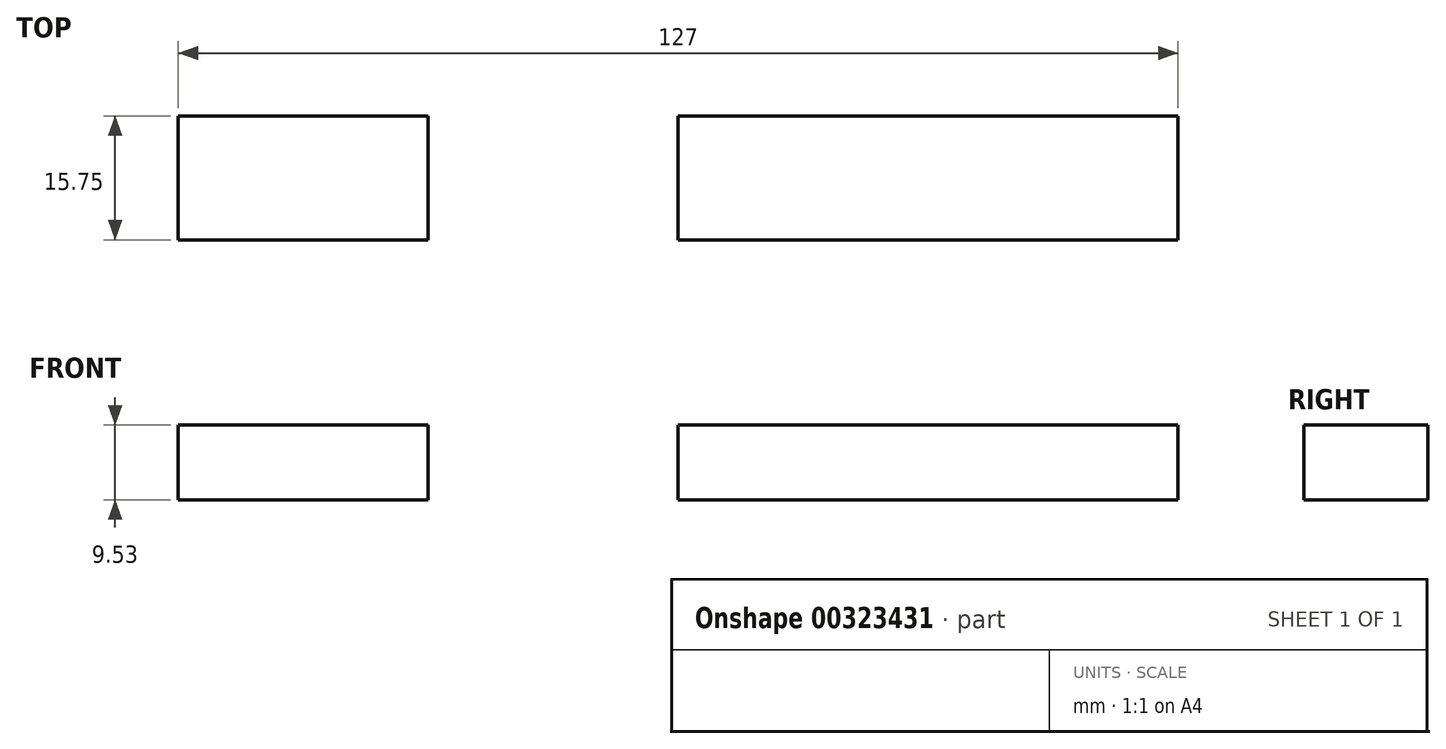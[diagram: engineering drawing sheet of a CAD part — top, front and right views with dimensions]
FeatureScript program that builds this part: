
annotation { "Feature Type Name" : "Feature", "Feature Type Description" : "" }
export const myFeature = defineFeature(function(context is Context, id is Id, definition is map)
    precondition{}
    {
        {
            var Q0;
            Q0=qCreatedBy(makeId("Front.planeOp"),FACE);
            var sketch = newSketch(context, id + "F0", { "sketchPlane" : qUnion([Q0])});
            skLineSegment(sketch, "E0.bottom", {"start": v(0, 0) * mm, "end": v(127, 0) * mm});
            skLineSegment(sketch, "E0.top", {"start": v(0, 177.8) * mm, "end": v(127, 177.8) * mm});
            skLineSegment(sketch, "E0.left", {"start": v(0, 0) * mm, "end": v(0, 177.8) * mm});
            skLineSegment(sketch, "E0.right", {"start": v(127, 0) * mm, "end": v(127, 177.8) * mm});
            skLineSegment(sketch, "E1", {"start": v(0, 9.53) * mm, "end": v(127, 9.53) * mm});
            skLineSegment(sketch, "E2", {"start": v(127, 9.52) * mm, "end": v(127, 19.05) * mm});
            skLineSegment(sketch, "E3", {"start": v(127, 19.05) * mm, "end": v(0, 19.05) * mm});
            skLineSegment(sketch, "E4", {"start": v(0, 19.05) * mm, "end": v(0, 28.57) * mm});
            skLineSegment(sketch, "E5", {"start": v(0, 28.57) * mm, "end": v(127, 28.57) * mm});
            skLineSegment(sketch, "E6", {"start": v(127, 28.57) * mm, "end": v(127, 38.1) * mm});
            skLineSegment(sketch, "E7", {"start": v(127, 38.1) * mm, "end": v(0, 38.1) * mm});
            skLineSegment(sketch, "E8", {"start": v(0, 38.1) * mm, "end": v(0, 47.62) * mm});
            skLineSegment(sketch, "E9", {"start": v(0, 47.62) * mm, "end": v(127, 47.62) * mm});
            skLineSegment(sketch, "E10", {"start": v(0, 0) * mm, "end": v(0, 9.53) * mm});
            skLineSegment(sketch, "E11", {"start": v(0, 47.62) * mm, "end": v(0, 57.15) * mm});
            skLineSegment(sketch, "E12", {"start": v(0, 57.15) * mm, "end": v(127, 57.15) * mm});
            skLineSegment(sketch, "E13", {"start": v(127, 57.15) * mm, "end": v(127, 66.68) * mm});
            skLineSegment(sketch, "E14", {"start": v(127, 66.68) * mm, "end": v(0, 66.67) * mm});
            skLineSegment(sketch, "E15", {"start": v(0, 66.67) * mm, "end": v(0, 76.2) * mm});
            skLineSegment(sketch, "E16", {"start": v(0, 76.2) * mm, "end": v(127, 76.2) * mm});
            skLineSegment(sketch, "E17", {"start": v(127, 76.2) * mm, "end": v(127, 85.73) * mm});
            skLineSegment(sketch, "E18", {"start": v(127, 85.73) * mm, "end": v(0, 85.72) * mm});
            skLineSegment(sketch, "E19", {"start": v(0, 85.72) * mm, "end": v(0, 95.25) * mm});
            skLineSegment(sketch, "E20", {"start": v(0, 95.25) * mm, "end": v(127, 95.25) * mm});
            skLineSegment(sketch, "E21", {"start": v(127, 95.25) * mm, "end": v(127, 104.78) * mm});
            skLineSegment(sketch, "E22", {"start": v(127, 104.78) * mm, "end": v(0, 104.78) * mm});
            skLineSegment(sketch, "E23", {"start": v(0, 104.78) * mm, "end": v(0, 114.3) * mm});
            skLineSegment(sketch, "E24", {"start": v(0, 114.3) * mm, "end": v(127, 114.3) * mm});
            skLineSegment(sketch, "E25", {"start": v(127, 114.3) * mm, "end": v(127, 123.83) * mm});
            skLineSegment(sketch, "E26", {"start": v(127, 123.83) * mm, "end": v(0, 123.83) * mm});
            skLineSegment(sketch, "E27", {"start": v(0, 123.83) * mm, "end": v(0, 133.35) * mm});
            skLineSegment(sketch, "E28", {"start": v(0, 133.35) * mm, "end": v(127, 133.35) * mm});
            skLineSegment(sketch, "E29", {"start": v(0, 133.35) * mm, "end": v(0, 142.88) * mm});
            skLineSegment(sketch, "E30", {"start": v(0, 142.88) * mm, "end": v(127, 142.88) * mm});
            skLineSegment(sketch, "E31", {"start": v(127, 142.88) * mm, "end": v(127, 152.4) * mm});
            skLineSegment(sketch, "E32", {"start": v(127, 152.4) * mm, "end": v(0, 152.4) * mm});
            skLineSegment(sketch, "E33", {"start": v(0, 152.4) * mm, "end": v(0, 161.93) * mm});
            skLineSegment(sketch, "E34", {"start": v(0, 161.93) * mm, "end": v(127, 161.93) * mm});
            skLineSegment(sketch, "E35", {"start": v(127, 161.93) * mm, "end": v(127, 171.45) * mm});
            skLineSegment(sketch, "E36", {"start": v(127, 171.45) * mm, "end": v(0, 171.45) * mm});
            skLineSegment(sketch, "E37", {"start": v(0, 171.45) * mm, "end": v(0, 177.8) * mm});
            skLineSegment(sketch, "E38", {"start": v(63.5, 0) * mm, "end": v(63.5, 9.53) * mm});
            skLineSegment(sketch, "E39", {"start": v(63.5, 19.05) * mm, "end": v(63.5, 28.57) * mm});
            skLineSegment(sketch, "E40", {"start": v(63.5, 38.1) * mm, "end": v(63.5, 47.62) * mm});
            skLineSegment(sketch, "E41", {"start": v(63.5, 57.15) * mm, "end": v(63.5, 66.67) * mm});
            skLineSegment(sketch, "E42", {"start": v(63.5, 76.2) * mm, "end": v(63.5, 85.73) * mm});
            skLineSegment(sketch, "E43", {"start": v(63.5, 95.25) * mm, "end": v(63.5, 104.78) * mm});
            skLineSegment(sketch, "E44", {"start": v(63.5, 114.3) * mm, "end": v(63.5, 123.83) * mm});
            skLineSegment(sketch, "E45", {"start": v(63.5, 133.35) * mm, "end": v(63.5, 142.88) * mm});
            skLineSegment(sketch, "E46", {"start": v(63.5, 152.4) * mm, "end": v(63.5, 161.93) * mm});
            skLineSegment(sketch, "E47", {"start": v(63.5, 171.45) * mm, "end": v(63.5, 177.8) * mm});
            skLineSegment(sketch, "E48", {"start": v(63.5, 9.53) * mm, "end": v(0, 9.53) * mm});
            skLineSegment(sketch, "E49", {"start": v(63.5, 9.53) * mm, "end": v(127, 9.53) * mm});
            skLineSegment(sketch, "E50", {"start": v(31.75, 9.53) * mm, "end": v(31.75, 0) * mm});
            skLineSegment(sketch, "E51", {"start": v(95.25, 9.53) * mm, "end": v(95.25, 0) * mm});
            skLineSegment(sketch, "E52", {"start": v(95.25, 19.05) * mm, "end": v(95.25, 28.57) * mm});
            skLineSegment(sketch, "E53", {"start": v(95.25, 38.1) * mm, "end": v(95.25, 47.62) * mm});
            skLineSegment(sketch, "E54", {"start": v(95.25, 57.15) * mm, "end": v(95.25, 66.67) * mm});
            skLineSegment(sketch, "E55", {"start": v(95.25, 76.2) * mm, "end": v(95.25, 85.73) * mm});
            skLineSegment(sketch, "E56", {"start": v(95.25, 95.25) * mm, "end": v(95.25, 104.78) * mm});
            skLineSegment(sketch, "E57", {"start": v(95.25, 114.3) * mm, "end": v(95.25, 123.83) * mm});
            skLineSegment(sketch, "E58", {"start": v(95.25, 133.35) * mm, "end": v(95.25, 142.88) * mm});
            skLineSegment(sketch, "E59", {"start": v(95.25, 152.4) * mm, "end": v(95.25, 161.93) * mm});
            skLineSegment(sketch, "E60", {"start": v(95.25, 171.45) * mm, "end": v(95.25, 177.8) * mm});
            skLineSegment(sketch, "E61", {"start": v(31.75, 19.05) * mm, "end": v(31.75, 28.57) * mm});
            skLineSegment(sketch, "E62", {"start": v(31.75, 38.1) * mm, "end": v(31.75, 47.62) * mm});
            skLineSegment(sketch, "E63", {"start": v(31.75, 57.15) * mm, "end": v(31.75, 66.67) * mm});
            skLineSegment(sketch, "E64", {"start": v(31.75, 76.2) * mm, "end": v(31.75, 85.73) * mm});
            skLineSegment(sketch, "E65", {"start": v(31.75, 95.25) * mm, "end": v(31.75, 104.78) * mm});
            skLineSegment(sketch, "E66", {"start": v(31.75, 114.3) * mm, "end": v(31.75, 123.83) * mm});
            skLineSegment(sketch, "E67", {"start": v(31.75, 133.35) * mm, "end": v(31.75, 142.88) * mm});
            skLineSegment(sketch, "E68", {"start": v(31.75, 152.4) * mm, "end": v(31.75, 161.93) * mm});
            skLineSegment(sketch, "E69", {"start": v(31.75, 171.45) * mm, "end": v(31.75, 177.8) * mm});
            skLineSegment(sketch, "E70", {"start": v(31.75, 9.53) * mm, "end": v(63.5, 9.53) * mm});
            skLineSegment(sketch, "E71", {"start": v(47.62, 9.53) * mm, "end": v(47.62, 19.05) * mm});
            skLineSegment(sketch, "E72", {"start": v(47.62, 28.57) * mm, "end": v(47.62, 38.1) * mm});
            skLineSegment(sketch, "E73", {"start": v(47.62, 47.62) * mm, "end": v(47.62, 57.15) * mm});
            skLineSegment(sketch, "E74", {"start": v(47.62, 66.67) * mm, "end": v(47.62, 76.2) * mm});
            skLineSegment(sketch, "E75", {"start": v(47.62, 85.72) * mm, "end": v(47.62, 95.25) * mm});
            skLineSegment(sketch, "E76", {"start": v(47.62, 104.78) * mm, "end": v(47.62, 114.3) * mm});
            skLineSegment(sketch, "E77", {"start": v(47.62, 123.83) * mm, "end": v(47.62, 133.35) * mm});
            skLineSegment(sketch, "E78", {"start": v(47.62, 142.88) * mm, "end": v(47.62, 152.4) * mm});
            skLineSegment(sketch, "E79", {"start": v(47.62, 161.93) * mm, "end": v(47.62, 171.45) * mm});
            skSolve(sketch);
        }
        {
            var Q0;
            Q0=makeQuery(id+"F0.imprint","IMPRINT",FACE,{"disambiguationData":[TD([[makeQuery(id+"F0.imprint","IMPRINT",EDGE,{"derivedFrom":sQuery(id+"F0.wireOp",EDGE,"E0.bottom")}),1.0]])]});
            extrude(context, id + "F1", {"entities" : qUnion([Q0]), "depth" : 15.75 * mm});
        }
    });
